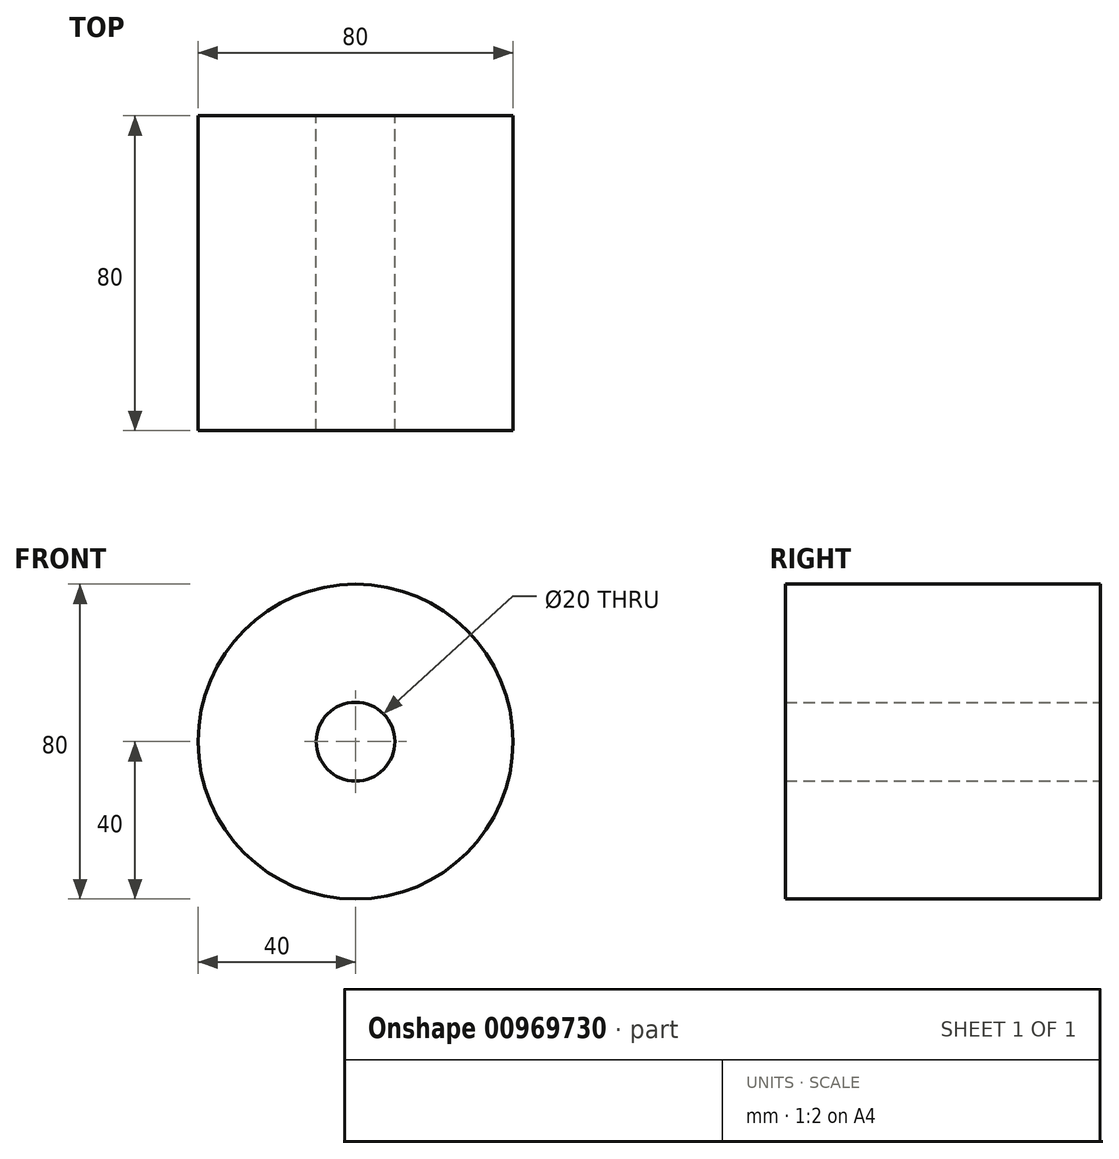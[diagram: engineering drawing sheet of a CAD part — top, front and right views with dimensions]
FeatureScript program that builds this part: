
annotation { "Feature Type Name" : "Feature", "Feature Type Description" : "" }
export const myFeature = defineFeature(function(context is Context, id is Id, definition is map)
    precondition{}
    {
        {
            var Q0;
            Q0=qCreatedBy(makeId("Front.planeOp"),FACE);
            var sketch = newSketch(context, id + "F0", { "sketchPlane" : qUnion([Q0])});
            skCircle(sketch, "E0", {"center": v(0, 0) * mm, "radius": 40 * mm});
            skCircle(sketch, "E1", {"center": v(0, 0) * mm, "radius": 10 * mm});
            skSolve(sketch);
        }
        {
            var Q0;
            Q0 = qSketchRegion(id + "F0", true);
            extrude(context, id + "F1", {"entities" : qUnion([Q0]), "depth" : 80 * mm, "offsetDistance" : 25 * mm});
        }
    });
